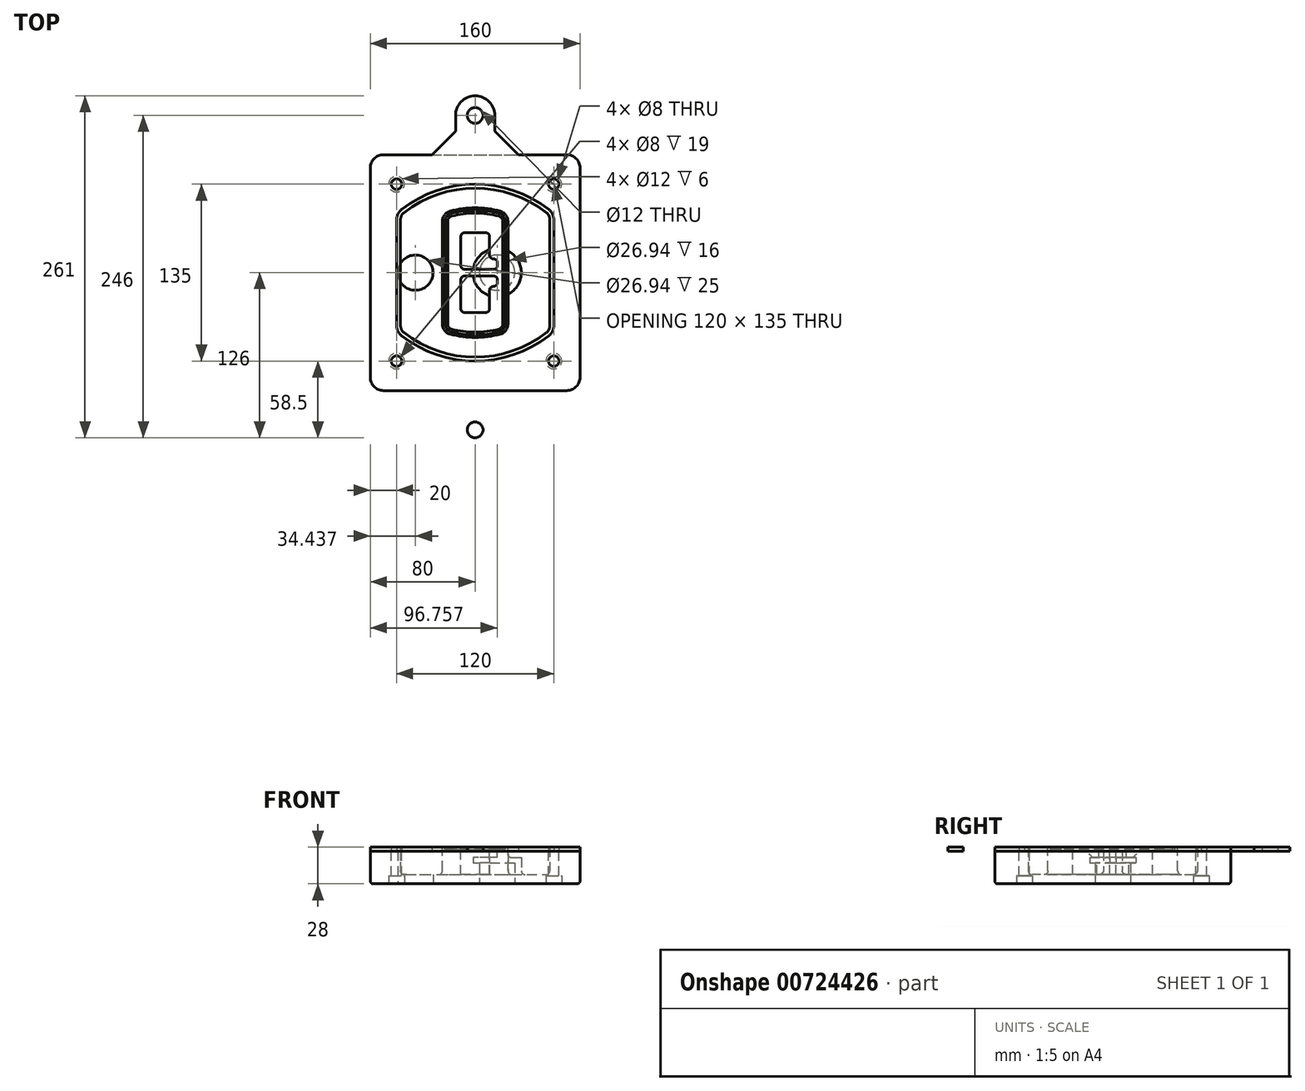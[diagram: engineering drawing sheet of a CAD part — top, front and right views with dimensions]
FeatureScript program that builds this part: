
annotation { "Feature Type Name" : "Feature", "Feature Type Description" : "" }
export const myFeature = defineFeature(function(context is Context, id is Id, definition is map)
    precondition{}
    {
        {
            var Q0;
            Q0=qCreatedBy(makeId("Top.planeOp"),FACE);
            var sketch = newSketch(context, id + "F0", { "sketchPlane" : qUnion([Q0])});
            skPoint(sketch, "E0.rect.middle", {"position": v(0, 0) * mm});
            skLineSegment(sketch, "E1.bottom", {"start": v(-70, -90) * mm, "end": v(70, -90) * mm});
            skLineSegment(sketch, "E1.top", {"start": v(-70, 90) * mm, "end": v(70, 90) * mm});
            skLineSegment(sketch, "E1.left", {"start": v(-80, -80) * mm, "end": v(-80, 80) * mm});
            skLineSegment(sketch, "E1.right", {"start": v(80, -80) * mm, "end": v(80, 80) * mm});
            skLineSegment(sketch, "E2", {"start": v(-80, 90) * mm, "end": v(80, -90) * mm, "construction": true});
            skLineSegment(sketch, "E3", {"start": v(80, 90) * mm, "end": v(-80, -90) * mm, "construction": true});
            skCircle(sketch, "E4", {"center": v(-60, 67.5) * mm, "radius": 4 * mm});
            skCircle(sketch, "E5", {"center": v(60, 67.5) * mm, "radius": 4 * mm});
            skCircle(sketch, "E6", {"center": v(60, -67.5) * mm, "radius": 4 * mm});
            skCircle(sketch, "E7", {"center": v(-60, -67.5) * mm, "radius": 4 * mm});
            skLineSegment(sketch, "E8", {"start": v(-60, 67.5) * mm, "end": v(60, 67.5) * mm, "construction": true});
            skLineSegment(sketch, "E9", {"start": v(60, 67.5) * mm, "end": v(60, -67.5) * mm, "construction": true});
            skLineSegment(sketch, "E10", {"start": v(60, -67.5) * mm, "end": v(-60, -67.5) * mm, "construction": true});
            skLineSegment(sketch, "E11", {"start": v(-60, -67.5) * mm, "end": v(-60, 67.5) * mm, "construction": true});
            skLineSegment(sketch, "E12", {"start": v(-60, 40.3) * mm, "end": v(-60, -40.3) * mm});
            skLineSegment(sketch, "E13", {"start": v(60, 40.3) * mm, "end": v(60, -40.3) * mm});
            skArc(sketch, "E14", {"start": v(56.15, 48.18) * mm, "mid": v(0, 67.5) * mm, "end": v(-56.15, 48.18) * mm});
            skArc(sketch, "E15", {"start": v(-56.15, -48.18) * mm, "mid": v(0, -67.5) * mm, "end": v(56.15, -48.18) * mm});
            skLineSegment(sketch, "E16", {"start": v(-60, 0) * mm, "end": v(60, 0) * mm, "construction": true});
            skPoint(sketch, "E17.visualSharp", {"position": v(-60, -45) * mm});
            skArc(sketch, "E17.filletArc", {"start": v(-60, -40.3) * mm, "mid": v(-58.99, -44.68) * mm, "end": v(-56.15, -48.18) * mm});
            skPoint(sketch, "E18.visualSharp", {"position": v(-60, 45) * mm});
            skArc(sketch, "E18.filletArc", {"start": v(-56.15, 48.18) * mm, "mid": v(-58.99, 44.68) * mm, "end": v(-60, 40.3) * mm});
            skPoint(sketch, "E19.visualSharp", {"position": v(60, 45) * mm});
            skArc(sketch, "E19.filletArc", {"start": v(60, 40.3) * mm, "mid": v(58.99, 44.68) * mm, "end": v(56.15, 48.18) * mm});
            skPoint(sketch, "E20.visualSharp", {"position": v(60, -45) * mm});
            skArc(sketch, "E20.filletArc", {"start": v(56.15, -48.18) * mm, "mid": v(58.99, -44.68) * mm, "end": v(60, -40.3) * mm});
            skPoint(sketch, "E21.visualSharp", {"position": v(-80, 90) * mm});
            skArc(sketch, "E21.filletArc", {"start": v(-70, 90) * mm, "mid": v(-77.07, 87.07) * mm, "end": v(-80, 80) * mm});
            skPoint(sketch, "E22.visualSharp", {"position": v(80, 90) * mm});
            skArc(sketch, "E22.filletArc", {"start": v(80, 80) * mm, "mid": v(77.07, 87.07) * mm, "end": v(70, 90) * mm});
            skPoint(sketch, "E23.visualSharp", {"position": v(80, -90) * mm});
            skArc(sketch, "E23.filletArc", {"start": v(70, -90) * mm, "mid": v(77.07, -87.07) * mm, "end": v(80, -80) * mm});
            skPoint(sketch, "E24.visualSharp", {"position": v(-80, -90) * mm});
            skArc(sketch, "E24.filletArc", {"start": v(-80, -80) * mm, "mid": v(-77.07, -87.07) * mm, "end": v(-70, -90) * mm});
            skArc(sketch, "E25.0", {"start": v(57, 40.3) * mm, "mid": v(56.3, 43.36) * mm, "end": v(54.3, 45.81) * mm});
            skLineSegment(sketch, "E25.1", {"start": v(57, 40.3) * mm, "end": v(57, -40.3) * mm});
            skArc(sketch, "E25.2", {"start": v(54.3, -45.81) * mm, "mid": v(56.3, -43.36) * mm, "end": v(57, -40.3) * mm});
            skArc(sketch, "E25.3", {"start": v(-54.3, -45.81) * mm, "mid": v(0, -64.5) * mm, "end": v(54.3, -45.81) * mm});
            skArc(sketch, "E25.4", {"start": v(-57, -40.3) * mm, "mid": v(-56.3, -43.36) * mm, "end": v(-54.3, -45.81) * mm});
            skArc(sketch, "E25.5", {"start": v(54.3, 45.81) * mm, "mid": v(0, 64.5) * mm, "end": v(-54.3, 45.81) * mm});
            skLineSegment(sketch, "E25.6", {"start": v(-57, 40.3) * mm, "end": v(-57, -40.3) * mm});
            skArc(sketch, "E25.7", {"start": v(-54.3, 45.81) * mm, "mid": v(-56.3, 43.36) * mm, "end": v(-57, 40.3) * mm});
            skArc(sketch, "E26.0", {"start": v(-58.62, 51.33) * mm, "mid": v(-62.58, 46.43) * mm, "end": v(-64, 40.3) * mm});
            skArc(sketch, "E26.1", {"start": v(58.62, 51.33) * mm, "mid": v(0, 71.5) * mm, "end": v(-58.62, 51.33) * mm});
            skArc(sketch, "E26.2", {"start": v(64, 40.3) * mm, "mid": v(62.58, 46.43) * mm, "end": v(58.62, 51.33) * mm});
            skLineSegment(sketch, "E26.3", {"start": v(64, 40.3) * mm, "end": v(64, -40.3) * mm});
            skArc(sketch, "E26.4", {"start": v(58.62, -51.33) * mm, "mid": v(62.58, -46.43) * mm, "end": v(64, -40.3) * mm});
            skLineSegment(sketch, "E26.5", {"start": v(-64, 40.3) * mm, "end": v(-64, -40.3) * mm});
            skArc(sketch, "E26.6", {"start": v(-58.62, -51.33) * mm, "mid": v(0, -71.5) * mm, "end": v(58.62, -51.33) * mm});
            skArc(sketch, "E26.7", {"start": v(-64, -40.3) * mm, "mid": v(-62.58, -46.43) * mm, "end": v(-58.62, -51.33) * mm});
            skSolve(sketch);
        }
        {
            var Q0;
            Q0=makeQuery(id+"F0.imprint","IMPRINT",FACE,{"disambiguationData":[TD([[makeQuery(id+"F0.imprint","IMPRINT",EDGE,{"derivedFrom":sQuery(id+"F0.wireOp",EDGE,"E1.bottom")}),1.0]])]});
            var Q1;
            Q1=makeQuery(id+"F0.imprint","IMPRINT",FACE,{"disambiguationData":[TD([[makeQuery(id+"F0.imprint","IMPRINT",EDGE,{"derivedFrom":sQuery(id+"F0.wireOp",EDGE,"E12")}),1.0]])]});
            var Q2;
            Q2=makeQuery(id+"F0.imprint","IMPRINT",FACE,{"disambiguationData":[TD([[makeQuery(id+"F0.imprint","IMPRINT",EDGE,{"derivedFrom":sQuery(id+"F0.wireOp",EDGE,"E25.0")}),1.0]])]});
            var Q3;
            Q3=makeQuery(id+"F0.imprint","IMPRINT",FACE,{"disambiguationData":[TD([[makeQuery(id+"F0.imprint","IMPRINT",EDGE,{"derivedFrom":sQuery(id+"F0.wireOp",EDGE,"E12")}),-1.0]])]});
            extrude(context, id + "F1", {"entities" : qUnion([Q0, Q1, Q2, Q3]), "oppositeDirection" : true, "depth" : 25 * mm});
        }
        {
            var Q0;
            Q0=makeQuery(id+"F0.imprint","IMPRINT",FACE,{"disambiguationData":[TD([[makeQuery(id+"F0.imprint","IMPRINT",EDGE,{"derivedFrom":sQuery(id+"F0.wireOp",EDGE,"E12")}),1.0]])]});
            extrude(context, id + "F2", {"entities" : qUnion([Q0]), "operationType" : NewBodyOperationType.ADD, "depth" : 3 * mm});
        }
        {
            var Q0;
            Q0=makeQuery(id+"F0.imprint","IMPRINT",FACE,{"disambiguationData":[TD([[makeQuery(id+"F0.imprint","IMPRINT",EDGE,{"derivedFrom":sQuery(id+"F0.wireOp",EDGE,"E25.0")}),1.0]])]});
            extrude(context, id + "F3", {"entities" : qUnion([Q0]), "operationType" : NewBodyOperationType.REMOVE, "oppositeDirection" : true, "depth" : 18 * mm});
        }
        {
            var Q0;
            Q0=makeQuery(id+"F2.opExtrude","CAP_FACE",FACE,{"disambiguationData":[OSD([sQuery(id+"F0.wireOp",EDGE,"E12"),sQuery(id+"F0.wireOp",EDGE,"E13"),sQuery(id+"F0.wireOp",EDGE,"E14"),sQuery(id+"F0.wireOp",EDGE,"E15"),sQuery(id+"F0.wireOp",EDGE,"E17.filletArc"),sQuery(id+"F0.wireOp",EDGE,"E18.filletArc"),sQuery(id+"F0.wireOp",EDGE,"E19.filletArc"),sQuery(id+"F0.wireOp",EDGE,"E20.filletArc"),sQuery(id+"F0.wireOp",EDGE,"E25.0"),sQuery(id+"F0.wireOp",EDGE,"E25.1"),sQuery(id+"F0.wireOp",EDGE,"E25.2"),sQuery(id+"F0.wireOp",EDGE,"E25.3"),sQuery(id+"F0.wireOp",EDGE,"E25.4"),sQuery(id+"F0.wireOp",EDGE,"E25.5"),sQuery(id+"F0.wireOp",EDGE,"E25.6"),sQuery(id+"F0.wireOp",EDGE,"E25.7")])],"isStart":false});
            var sketch = newSketch(context, id + "F4", { "sketchPlane" : qUnion([Q0])});
            skArc(sketch, "E27.0", {"start": v(-19.08, -46.97) * mm, "mid": v(0, -49.5) * mm, "end": v(19.08, -46.97) * mm});
            skArc(sketch, "E28.0", {"start": v(19.08, 46.97) * mm, "mid": v(0, 49.5) * mm, "end": v(-19.08, 46.97) * mm});
            skLineSegment(sketch, "E29", {"start": v(-25, 39.25) * mm, "end": v(-25, -39.25) * mm});
            skLineSegment(sketch, "E30", {"start": v(25, 39.25) * mm, "end": v(25, -39.25) * mm});
            skLineSegment(sketch, "E31", {"start": v(-25, 45.1) * mm, "end": v(25, 45.1) * mm, "construction": true});
            skLineSegment(sketch, "E32", {"start": v(-25, -45.1) * mm, "end": v(25, -45.1) * mm, "construction": true});
            skPoint(sketch, "E33.visualSharp", {"position": v(-25, 45.1) * mm});
            skArc(sketch, "E33.filletArc", {"start": v(-19.08, 46.97) * mm, "mid": v(-23.35, 44.11) * mm, "end": v(-25, 39.25) * mm});
            skPoint(sketch, "E34.visualSharp", {"position": v(25, 45.1) * mm});
            skArc(sketch, "E34.filletArc", {"start": v(25, 39.25) * mm, "mid": v(23.35, 44.11) * mm, "end": v(19.08, 46.97) * mm});
            skPoint(sketch, "E35.visualSharp", {"position": v(25, -45.1) * mm});
            skArc(sketch, "E35.filletArc", {"start": v(19.08, -46.97) * mm, "mid": v(23.35, -44.11) * mm, "end": v(25, -39.25) * mm});
            skPoint(sketch, "E36.visualSharp", {"position": v(-25, -45.1) * mm});
            skArc(sketch, "E36.filletArc", {"start": v(-25, -39.25) * mm, "mid": v(-23.35, -44.11) * mm, "end": v(-19.08, -46.97) * mm});
            skArc(sketch, "E37.0", {"start": v(54.3, 45.81) * mm, "mid": v(0, 64.5) * mm, "end": v(-54.3, 45.81) * mm});
            skArc(sketch, "E37.1", {"start": v(-54.3, 45.81) * mm, "mid": v(-56.3, 43.36) * mm, "end": v(-57, 40.3) * mm});
            skLineSegment(sketch, "E37.2", {"start": v(-57, 40.3) * mm, "end": v(-57, -40.3) * mm});
            skArc(sketch, "E37.3", {"start": v(-57, -40.3) * mm, "mid": v(-56.3, -43.36) * mm, "end": v(-54.3, -45.81) * mm});
            skArc(sketch, "E37.4", {"start": v(-54.3, -45.81) * mm, "mid": v(0, -64.5) * mm, "end": v(54.3, -45.81) * mm});
            skArc(sketch, "E37.5", {"start": v(54.3, -45.81) * mm, "mid": v(56.3, -43.36) * mm, "end": v(57, -40.3) * mm});
            skLineSegment(sketch, "E37.6", {"start": v(57, 40.3) * mm, "end": v(57, -40.3) * mm});
            skArc(sketch, "E37.7", {"start": v(57, 40.3) * mm, "mid": v(56.3, 43.36) * mm, "end": v(54.3, 45.81) * mm});
            skLineSegment(sketch, "E38.0", {"start": v(23, 39.25) * mm, "end": v(23, -39.25) * mm});
            skArc(sketch, "E38.1", {"start": v(18.56, -45.04) * mm, "mid": v(21.76, -42.9) * mm, "end": v(23, -39.25) * mm});
            skArc(sketch, "E38.2", {"start": v(-18.56, -45.04) * mm, "mid": v(0, -47.5) * mm, "end": v(18.56, -45.04) * mm});
            skArc(sketch, "E38.3", {"start": v(-23, -39.25) * mm, "mid": v(-21.76, -42.9) * mm, "end": v(-18.56, -45.04) * mm});
            skLineSegment(sketch, "E38.4", {"start": v(-23, 39.25) * mm, "end": v(-23, -39.25) * mm});
            skArc(sketch, "E38.5", {"start": v(23, 39.25) * mm, "mid": v(21.76, 42.9) * mm, "end": v(18.56, 45.04) * mm});
            skArc(sketch, "E38.6", {"start": v(-18.56, 45.04) * mm, "mid": v(-21.76, 42.9) * mm, "end": v(-23, 39.25) * mm});
            skArc(sketch, "E38.7", {"start": v(18.56, 45.04) * mm, "mid": v(0, 47.5) * mm, "end": v(-18.56, 45.04) * mm});
            skArc(sketch, "E39.0", {"start": v(21, 39.25) * mm, "mid": v(20.18, 41.68) * mm, "end": v(18.04, 43.1) * mm});
            skLineSegment(sketch, "E39.1", {"start": v(21, 39.25) * mm, "end": v(21, -39.25) * mm});
            skArc(sketch, "E39.2", {"start": v(18.04, -43.1) * mm, "mid": v(20.18, -41.68) * mm, "end": v(21, -39.25) * mm});
            skArc(sketch, "E39.3", {"start": v(-18.04, -43.1) * mm, "mid": v(0, -45.5) * mm, "end": v(18.04, -43.1) * mm});
            skArc(sketch, "E39.4", {"start": v(-21, -39.25) * mm, "mid": v(-20.18, -41.68) * mm, "end": v(-18.04, -43.1) * mm});
            skArc(sketch, "E39.5", {"start": v(18.04, 43.1) * mm, "mid": v(0, 45.5) * mm, "end": v(-18.04, 43.1) * mm});
            skLineSegment(sketch, "E39.6", {"start": v(-21, 39.25) * mm, "end": v(-21, -39.25) * mm});
            skArc(sketch, "E39.7", {"start": v(-18.04, 43.1) * mm, "mid": v(-20.18, 41.68) * mm, "end": v(-21, 39.25) * mm});
            skLineSegment(sketch, "E40", {"start": v(-25, 0) * mm, "end": v(25, 0) * mm, "construction": true});
            skLineSegment(sketch, "E41", {"start": v(-11, 5.5) * mm, "end": v(-11, 27.5) * mm});
            skLineSegment(sketch, "E42", {"start": v(-8, 30.5) * mm, "end": v(8, 30.5) * mm});
            skLineSegment(sketch, "E43", {"start": v(11, 27.5) * mm, "end": v(11, 13.5) * mm});
            skLineSegment(sketch, "E44", {"start": v(14, 10.5) * mm, "end": v(14, 10.5) * mm});
            skLineSegment(sketch, "E45", {"start": v(17, 7.5) * mm, "end": v(17, 5.5) * mm});
            skLineSegment(sketch, "E46", {"start": v(14, 2.5) * mm, "end": v(-8, 2.5) * mm});
            skPoint(sketch, "E47.visualSharp", {"position": v(-11, 30.5) * mm});
            skArc(sketch, "E47.filletArc", {"start": v(-8, 30.5) * mm, "mid": v(-10.12, 29.62) * mm, "end": v(-11, 27.5) * mm});
            skPoint(sketch, "E48.visualSharp", {"position": v(11, 30.5) * mm});
            skArc(sketch, "E48.filletArc", {"start": v(11, 27.5) * mm, "mid": v(10.12, 29.62) * mm, "end": v(8, 30.5) * mm});
            skPoint(sketch, "E49.visualSharp", {"position": v(11, 10.5) * mm});
            skArc(sketch, "E49.filletArc", {"start": v(11, 13.5) * mm, "mid": v(11.88, 11.38) * mm, "end": v(14, 10.5) * mm});
            skPoint(sketch, "E50.visualSharp", {"position": v(17, 10.5) * mm});
            skArc(sketch, "E50.filletArc", {"start": v(17, 7.5) * mm, "mid": v(16.12, 9.62) * mm, "end": v(14, 10.5) * mm});
            skPoint(sketch, "E51.visualSharp", {"position": v(17, 2.5) * mm});
            skArc(sketch, "E51.filletArc", {"start": v(14, 2.5) * mm, "mid": v(16.12, 3.38) * mm, "end": v(17, 5.5) * mm});
            skPoint(sketch, "E52.visualSharp", {"position": v(-11, 2.5) * mm});
            skArc(sketch, "E52.filletArc", {"start": v(-11, 5.5) * mm, "mid": v(-10.12, 3.38) * mm, "end": v(-8, 2.5) * mm});
            skLineSegment(sketch, "E53.0.MirrorCS", {"start": v(14, -2.5) * mm, "end": v(-8, -2.5) * mm});
            skArc(sketch, "E54.0.MirrorCS", {"start": v(-11, -5.5) * mm, "mid": v(-10.12, -3.38) * mm, "end": v(-8, -2.5) * mm});
            skLineSegment(sketch, "E55.0.MirrorCS", {"start": v(-11, -5.5) * mm, "end": v(-11, -27.5) * mm});
            skArc(sketch, "E56.0.MirrorCS", {"start": v(-8, -30.5) * mm, "mid": v(-10.12, -29.62) * mm, "end": v(-11, -27.5) * mm});
            skLineSegment(sketch, "E57.0.MirrorCS", {"start": v(-8, -30.5) * mm, "end": v(8, -30.5) * mm});
            skArc(sketch, "E58.0.MirrorCS", {"start": v(11, -27.5) * mm, "mid": v(10.12, -29.62) * mm, "end": v(8, -30.5) * mm});
            skLineSegment(sketch, "E59.0.MirrorCS", {"start": v(11, -27.5) * mm, "end": v(11, -13.5) * mm});
            skArc(sketch, "E60.0.MirrorCS", {"start": v(11, -13.5) * mm, "mid": v(11.88, -11.38) * mm, "end": v(14, -10.5) * mm});
            skArc(sketch, "E61.0.MirrorCS", {"start": v(17, -7.5) * mm, "mid": v(16.12, -9.62) * mm, "end": v(14, -10.5) * mm});
            skLineSegment(sketch, "E62.0.MirrorCS", {"start": v(17, -7.5) * mm, "end": v(17, -5.5) * mm});
            skArc(sketch, "E63.0.MirrorCS", {"start": v(14, -2.5) * mm, "mid": v(16.12, -3.38) * mm, "end": v(17, -5.5) * mm});
            skSolve(sketch);
        }
        {
            var Q0;
            Q0=makeQuery(id+"F4.imprint","IMPRINT",FACE,{"disambiguationData":[TD([[makeQuery(id+"F4.imprint","IMPRINT",EDGE,{"derivedFrom":sQuery(id+"F4.wireOp",EDGE,"E27.0")}),1.0]])]});
            var Q1;
            Q1=makeQuery(id+"F4.imprint","IMPRINT",FACE,{"disambiguationData":[TD([[makeQuery(id+"F4.imprint","IMPRINT",EDGE,{"derivedFrom":sQuery(id+"F4.wireOp",EDGE,"E38.0")}),-1.0]])]});
            var Q2;
            Q2=makeQuery(id+"F4.imprint","IMPRINT",FACE,{"disambiguationData":[TD([[makeQuery(id+"F4.imprint","IMPRINT",EDGE,{"derivedFrom":sQuery(id+"F4.wireOp",EDGE,"E39.0")}),1.0]])]});
            extrude(context, id + "F5", {"entities" : qUnion([Q0, Q1, Q2]), "operationType" : NewBodyOperationType.ADD, "endBound" : BoundingType.UP_TO_NEXT, "oppositeDirection" : true, "depth" : 25 * mm});
        }
        {
            var Q0;
            Q0=makeQuery(id+"F4.imprint","IMPRINT",FACE,{"disambiguationData":[TD([[makeQuery(id+"F4.imprint","IMPRINT",EDGE,{"derivedFrom":sQuery(id+"F4.wireOp",EDGE,"E38.0")}),-1.0]])]});
            extrude(context, id + "F6", {"entities" : qUnion([Q0]), "operationType" : NewBodyOperationType.REMOVE, "oppositeDirection" : true, "depth" : 2 * mm});
        }
        {
            var Q0;
            Q0=makeQuery(id+"F1.opExtrude","CAP_FACE",FACE,{"disambiguationData":[OSD([sQuery(id+"F0.wireOp",EDGE,"E1.bottom"),sQuery(id+"F0.wireOp",EDGE,"E1.top"),sQuery(id+"F0.wireOp",EDGE,"E1.left"),sQuery(id+"F0.wireOp",EDGE,"E1.right"),sQuery(id+"F0.wireOp",EDGE,"E4"),sQuery(id+"F0.wireOp",EDGE,"E5"),sQuery(id+"F0.wireOp",EDGE,"E6"),sQuery(id+"F0.wireOp",EDGE,"E7"),sQuery(id+"F0.wireOp",EDGE,"E21.filletArc"),sQuery(id+"F0.wireOp",EDGE,"E22.filletArc"),sQuery(id+"F0.wireOp",EDGE,"E23.filletArc"),sQuery(id+"F0.wireOp",EDGE,"E24.filletArc")])],"isStart":false});
            var sketch = newSketch(context, id + "F7", { "sketchPlane" : qUnion([Q0])});
            skCircle(sketch, "E64", {"center": v(16.76, 0) * mm, "radius": 13.47 * mm});
            skCircle(sketch, "E65", {"center": v(-45.56, 0) * mm, "radius": 13.47 * mm});
            skLineSegment(sketch, "E66", {"start": v(80, 0) * mm, "end": v(-80, 0) * mm});
            skCircle(sketch, "E67", {"center": v(16.76, 0) * mm, "radius": 18.47 * mm});
            skCircle(sketch, "E68", {"center": v(60, -67.5) * mm, "radius": 6 * mm});
            skCircle(sketch, "E69", {"center": v(-60, -67.5) * mm, "radius": 6 * mm});
            skCircle(sketch, "E70", {"center": v(-60, 67.5) * mm, "radius": 6 * mm});
            skCircle(sketch, "E71", {"center": v(60, 67.5) * mm, "radius": 6 * mm});
            skSolve(sketch);
        }
        {
            var Q0;
            {var subQ1=sQuery(id+"F7.wireOp",EDGE,"E66");var subQ4=sQuery(id+"F7.wireOp",EDGE,"E64");var subQ6=makeQuery(id+"F7.imprint","INTERSECT",VERTEX,{"disambiguationData":[OD(0.0)],"derivedFrom":[subQ4,subQ1]});Q0=makeQuery(id+"F7.imprint","IMPRINT",FACE,{"disambiguationData":[TD([[makeQuery(id+"F7.imprint","IMPRINT",EDGE,{"disambiguationData":[TD([[subQ6,-1.0]])],"derivedFrom":subQ4}),-1.0]])]});}
            var Q1;
            {var subQ0=sQuery(id+"F7.wireOp",EDGE,"E66");var subQ1=sQuery(id+"F7.wireOp",EDGE,"E64");var subQ3=makeQuery(id+"F7.imprint","INTERSECT",VERTEX,{"disambiguationData":[OD(0.0)],"derivedFrom":[subQ1,subQ0]});Q1=makeQuery(id+"F7.imprint","IMPRINT",FACE,{"disambiguationData":[TD([[makeQuery(id+"F7.imprint","IMPRINT",EDGE,{"disambiguationData":[TD([[subQ3,-1.0]])],"derivedFrom":subQ1}),1.0]])]});}
            var Q2;
            {var subQ0=sQuery(id+"F7.wireOp",EDGE,"E66");var subQ1=sQuery(id+"F7.wireOp",EDGE,"E64");var subQ3=makeQuery(id+"F7.imprint","INTERSECT",VERTEX,{"disambiguationData":[OD(0.0)],"derivedFrom":[subQ1,subQ0]});Q2=makeQuery(id+"F7.imprint","IMPRINT",FACE,{"disambiguationData":[TD([[makeQuery(id+"F7.imprint","IMPRINT",EDGE,{"disambiguationData":[TD([[subQ3,1.0]])],"derivedFrom":subQ1}),1.0]])]});}
            var Q3;
            {var subQ1=sQuery(id+"F7.wireOp",EDGE,"E66");var subQ4=sQuery(id+"F7.wireOp",EDGE,"E64");var subQ6=makeQuery(id+"F7.imprint","INTERSECT",VERTEX,{"disambiguationData":[OD(0.0)],"derivedFrom":[subQ4,subQ1]});Q3=makeQuery(id+"F7.imprint","IMPRINT",FACE,{"disambiguationData":[TD([[makeQuery(id+"F7.imprint","IMPRINT",EDGE,{"disambiguationData":[TD([[subQ6,1.0]])],"derivedFrom":subQ4}),-1.0]])]});}
            extrude(context, id + "F8", {"entities" : qUnion([Q0, Q1, Q2, Q3]), "operationType" : NewBodyOperationType.ADD, "oppositeDirection" : true, "depth" : 20 * mm});
        }
        {
            var Q0;
            {var subQ0=sQuery(id+"F7.wireOp",EDGE,"E66");var subQ1=sQuery(id+"F7.wireOp",EDGE,"E64");var subQ3=makeQuery(id+"F7.imprint","INTERSECT",VERTEX,{"disambiguationData":[OD(0.0)],"derivedFrom":[subQ1,subQ0]});Q0=makeQuery(id+"F7.imprint","IMPRINT",FACE,{"disambiguationData":[TD([[makeQuery(id+"F7.imprint","IMPRINT",EDGE,{"disambiguationData":[TD([[subQ3,-1.0]])],"derivedFrom":subQ1}),1.0]])]});}
            var Q1;
            {var subQ0=sQuery(id+"F7.wireOp",EDGE,"E66");var subQ1=sQuery(id+"F7.wireOp",EDGE,"E64");var subQ3=makeQuery(id+"F7.imprint","INTERSECT",VERTEX,{"disambiguationData":[OD(0.0)],"derivedFrom":[subQ1,subQ0]});Q1=makeQuery(id+"F7.imprint","IMPRINT",FACE,{"disambiguationData":[TD([[makeQuery(id+"F7.imprint","IMPRINT",EDGE,{"disambiguationData":[TD([[subQ3,1.0]])],"derivedFrom":subQ1}),1.0]])]});}
            extrude(context, id + "F9", {"entities" : qUnion([Q0, Q1]), "operationType" : NewBodyOperationType.REMOVE, "oppositeDirection" : true, "depth" : 16 * mm});
        }
        {
            var Q0;
            {var subQ0=sQuery(id+"F7.wireOp",EDGE,"E66");var subQ1=sQuery(id+"F7.wireOp",EDGE,"E65");var subQ3=makeQuery(id+"F7.imprint","INTERSECT",VERTEX,{"disambiguationData":[OD(0.0)],"derivedFrom":[subQ1,subQ0]});Q0=makeQuery(id+"F7.imprint","IMPRINT",FACE,{"disambiguationData":[TD([[makeQuery(id+"F7.imprint","IMPRINT",EDGE,{"disambiguationData":[TD([[subQ3,-1.0]])],"derivedFrom":subQ1}),1.0]])]});}
            var Q1;
            {var subQ0=sQuery(id+"F7.wireOp",EDGE,"E66");var subQ1=sQuery(id+"F7.wireOp",EDGE,"E65");var subQ3=makeQuery(id+"F7.imprint","INTERSECT",VERTEX,{"disambiguationData":[OD(0.0)],"derivedFrom":[subQ1,subQ0]});Q1=makeQuery(id+"F7.imprint","IMPRINT",FACE,{"disambiguationData":[TD([[makeQuery(id+"F7.imprint","IMPRINT",EDGE,{"disambiguationData":[TD([[subQ3,1.0]])],"derivedFrom":subQ1}),1.0]])]});}
            extrude(context, id + "F10", {"entities" : qUnion([Q0, Q1]), "operationType" : NewBodyOperationType.REMOVE, "oppositeDirection" : true, "depth" : 25 * mm});
        }
        {
            var Q0;
            Q0=makeQuery(id+"F7.imprint","IMPRINT",FACE,{"disambiguationData":[TD([[makeQuery(id+"F7.imprint","IMPRINT",EDGE,{"derivedFrom":sQuery(id+"F7.wireOp",EDGE,"E68")}),1.0]])]});
            var Q1;
            Q1=makeQuery(id+"F7.imprint","IMPRINT",FACE,{"disambiguationData":[TD([[makeQuery(id+"F7.imprint","IMPRINT",EDGE,{"derivedFrom":makeQuery(id+"F1.opExtrude","CAP_EDGE",EDGE,{"disambiguationData":[OSD([sQuery(id+"F0.wireOp",EDGE,"E5")])],"isStart":false})}),-1.0]])]});
            var Q2;
            Q2=makeQuery(id+"F7.imprint","IMPRINT",FACE,{"disambiguationData":[TD([[makeQuery(id+"F7.imprint","IMPRINT",EDGE,{"derivedFrom":sQuery(id+"F7.wireOp",EDGE,"E69")}),1.0]])]});
            var Q3;
            Q3=makeQuery(id+"F7.imprint","IMPRINT",FACE,{"disambiguationData":[TD([[makeQuery(id+"F7.imprint","IMPRINT",EDGE,{"derivedFrom":makeQuery(id+"F1.opExtrude","CAP_EDGE",EDGE,{"disambiguationData":[OSD([sQuery(id+"F0.wireOp",EDGE,"E4")])],"isStart":false})}),-1.0]])]});
            var Q4;
            Q4=makeQuery(id+"F7.imprint","IMPRINT",FACE,{"disambiguationData":[TD([[makeQuery(id+"F7.imprint","IMPRINT",EDGE,{"derivedFrom":sQuery(id+"F7.wireOp",EDGE,"E70")}),1.0]])]});
            var Q5;
            Q5=makeQuery(id+"F7.imprint","IMPRINT",FACE,{"disambiguationData":[TD([[makeQuery(id+"F7.imprint","IMPRINT",EDGE,{"derivedFrom":makeQuery(id+"F1.opExtrude","CAP_EDGE",EDGE,{"disambiguationData":[OSD([sQuery(id+"F0.wireOp",EDGE,"E7")])],"isStart":false})}),-1.0]])]});
            var Q6;
            Q6=makeQuery(id+"F7.imprint","IMPRINT",FACE,{"disambiguationData":[TD([[makeQuery(id+"F7.imprint","IMPRINT",EDGE,{"derivedFrom":sQuery(id+"F7.wireOp",EDGE,"E71")}),1.0]])]});
            var Q7;
            Q7=makeQuery(id+"F7.imprint","IMPRINT",FACE,{"disambiguationData":[TD([[makeQuery(id+"F7.imprint","IMPRINT",EDGE,{"derivedFrom":makeQuery(id+"F1.opExtrude","CAP_EDGE",EDGE,{"disambiguationData":[OSD([sQuery(id+"F0.wireOp",EDGE,"E6")])],"isStart":false})}),-1.0]])]});
            extrude(context, id + "F11", {"entities" : qUnion([Q0, Q1, Q2, Q3, Q4, Q5, Q6, Q7]), "operationType" : NewBodyOperationType.REMOVE, "oppositeDirection" : true, "depth" : 6 * mm});
        }
        {
            var Q0;
            Q0=makeQuery(id+"F9.boolean.opBoolean","COPY",FACE,{"derivedFrom":makeQuery(id+"F9.opExtrude","CAP_FACE",FACE,{"disambiguationData":[OSD([sQuery(id+"F7.wireOp",EDGE,"E64")])],"isStart":false})});
            var sketch = newSketch(context, id + "F12", { "sketchPlane" : qUnion([Q0])});
            skArc(sketch, "E72.0", {"start": v(11, 17.55) * mm, "mid": v(2.57, 11.82) * mm, "end": v(-1.54, 2.5) * mm});
            skArc(sketch, "E72.1", {"start": v(-1.54, -2.5) * mm, "mid": v(2.57, -11.82) * mm, "end": v(11, -17.55) * mm});
            skLineSegment(sketch, "E73", {"start": v(-1.54, -2.5) * mm, "end": v(14, -2.5) * mm});
            skLineSegment(sketch, "E74.0", {"start": v(14, 2.5) * mm, "end": v(-1.54, 2.5) * mm});
            skArc(sketch, "E74.1", {"start": v(14, 2.5) * mm, "mid": v(16.12, 3.38) * mm, "end": v(17, 5.5) * mm});
            skLineSegment(sketch, "E74.2", {"start": v(17, 7.5) * mm, "end": v(17, 5.5) * mm});
            skArc(sketch, "E74.3", {"start": v(17, 7.5) * mm, "mid": v(16.12, 9.62) * mm, "end": v(14, 10.5) * mm});
            skArc(sketch, "E74.4", {"start": v(11, 13.5) * mm, "mid": v(11.88, 11.38) * mm, "end": v(14, 10.5) * mm});
            skLineSegment(sketch, "E74.5", {"start": v(11, 17.55) * mm, "end": v(11, 13.5) * mm});
            skLineSegment(sketch, "E74.7", {"start": v(14, -2.5) * mm, "end": v(-1.54, -2.5) * mm});
            skArc(sketch, "E74.8", {"start": v(14, -2.5) * mm, "mid": v(16.12, -3.38) * mm, "end": v(17, -5.5) * mm});
            skLineSegment(sketch, "E74.9", {"start": v(17, -7.5) * mm, "end": v(17, -5.5) * mm});
            skArc(sketch, "E74.10", {"start": v(17, -7.5) * mm, "mid": v(16.12, -9.62) * mm, "end": v(14, -10.5) * mm});
            skArc(sketch, "E74.11", {"start": v(11, -13.5) * mm, "mid": v(11.88, -11.38) * mm, "end": v(14, -10.5) * mm});
            skLineSegment(sketch, "E74.12", {"start": v(11, -17.55) * mm, "end": v(11, -13.5) * mm});
            skPoint(sketch, "E75.orphan", {"position": v(11, -27.5) * mm});
            skPoint(sketch, "E76.orphan", {"position": v(-8, -2.5) * mm});
            skPoint(sketch, "E77.orphan", {"position": v(-8, 2.5) * mm});
            skPoint(sketch, "E78.orphan", {"position": v(11, 27.5) * mm});
            skSolve(sketch);
        }
        {
            var Q0;
            {var subQ7=sQuery(id+"F12.wireOp",EDGE,"E72.0");var subQ14=sQuery(id+"F12.wireOp",EDGE,"E72.1");var subQ16=sQuery(id+"F12.wireOp",EDGE,"E74.1");var subQ18=sQuery(id+"F12.wireOp",EDGE,"E74.8");Q0=qUnion([makeQuery(id+"F12.imprint","IMPRINT",FACE,{"disambiguationData":[TD([[makeQuery(id+"F12.imprint","IMPRINT",EDGE,{"derivedFrom":subQ7}),1.0]])]}),makeQuery(id+"F12.imprint","IMPRINT",FACE,{"disambiguationData":[TD([[makeQuery(id+"F12.imprint","IMPRINT",EDGE,{"derivedFrom":subQ14}),1.0]])]}),makeQuery(id+"F12.imprint","IMPRINT",FACE,{"disambiguationData":[TD([[makeQuery(id+"F12.imprint","IMPRINT",EDGE,{"derivedFrom":subQ16}),1.0]])]}),makeQuery(id+"F12.imprint","IMPRINT",FACE,{"disambiguationData":[TD([[makeQuery(id+"F12.imprint","IMPRINT",EDGE,{"derivedFrom":subQ18}),-1.0]])]})]);}
            var Q1;
            Q1=makeQuery(id+"F5.boolean.opBoolean","SPLIT",FACE,{"disambiguationData":[TD([makeQuery(id+"F5.opExtrude","SWEPT_FACE",FACE,{"disambiguationData":[OSD([sQuery(id+"F4.wireOp",EDGE,"E41")])]})])],"derivedFrom":makeQuery(id+"F3.boolean.opBoolean","COPY",FACE,{"derivedFrom":makeQuery(id+"F3.opExtrude","CAP_FACE",FACE,{"disambiguationData":[OSD([sQuery(id+"F0.wireOp",EDGE,"E25.0"),sQuery(id+"F0.wireOp",EDGE,"E25.1"),sQuery(id+"F0.wireOp",EDGE,"E25.2"),sQuery(id+"F0.wireOp",EDGE,"E25.3"),sQuery(id+"F0.wireOp",EDGE,"E25.4"),sQuery(id+"F0.wireOp",EDGE,"E25.5"),sQuery(id+"F0.wireOp",EDGE,"E25.6"),sQuery(id+"F0.wireOp",EDGE,"E25.7")])],"isStart":false})})});
            extrude(context, id + "F13", {"entities" : qUnion([Q0]), "operationType" : NewBodyOperationType.REMOVE, "endBound" : BoundingType.UP_TO_SURFACE, "endBoundEntityFace" : qUnion([Q1]), "depth" : 25 * mm});
        }
        {
            var Q0;
            Q0=makeQuery(id+"F3.boolean.opBoolean","COPY",EDGE,{"derivedFrom":makeQuery(id+"F3.opExtrude","CAP_EDGE",EDGE,{"disambiguationData":[OSD([sQuery(id+"F0.wireOp",EDGE,"E25.6")])],"isStart":false})});
            var Q1;
            Q1=makeQuery(id+"F8.boolean.opBoolean","INTERSECT",EDGE,{"derivedFrom":[makeQuery(id+"F5.opExtrude","SWEPT_FACE",FACE,{"disambiguationData":[OSD([sQuery(id+"F4.wireOp",EDGE,"E30")])]}),makeQuery(id+"F8.opExtrude","CAP_FACE",FACE,{"disambiguationData":[OSD([sQuery(id+"F7.wireOp",EDGE,"E67")])],"isStart":false})]});
            var Q2;
            Q2=makeQuery(id+"F8.boolean.opBoolean","INTERSECT",EDGE,{"disambiguationData":[OD(1.0)],"derivedFrom":[makeQuery(id+"F5.opExtrude","SWEPT_FACE",FACE,{"disambiguationData":[OSD([sQuery(id+"F4.wireOp",EDGE,"E30")])]}),makeQuery(id+"F8.opExtrude","SWEPT_FACE",FACE,{"disambiguationData":[OSD([sQuery(id+"F7.wireOp",EDGE,"E67")])]})]});
            var Q3;
            {var subQ0=sQuery(id+"F4.wireOp",EDGE,"E30");Q3=makeQuery(id+"F8.boolean.opBoolean","SPLIT",EDGE,{"disambiguationData":[TD([makeQuery(id+"F5.opExtrude","SWEPT_FACE",FACE,{"disambiguationData":[OSD([sQuery(id+"F4.wireOp",EDGE,"E35.filletArc")])]})])],"derivedFrom":makeQuery(id+"F5.opExtrude","CAP_EDGE",EDGE,{"disambiguationData":[OSD([subQ0])],"isStart":false})});}
            var Q4;
            {var subQ0=sQuery(id+"F0.wireOp",EDGE,"E25.7");var subQ1=sQuery(id+"F0.wireOp",EDGE,"E25.1");var subQ2=sQuery(id+"F0.wireOp",EDGE,"E25.6");var subQ3=sQuery(id+"F0.wireOp",EDGE,"E25.5");var subQ4=sQuery(id+"F0.wireOp",EDGE,"E25.4");var subQ5=sQuery(id+"F0.wireOp",EDGE,"E25.0");var subQ6=sQuery(id+"F0.wireOp",EDGE,"E25.2");var subQ7=sQuery(id+"F0.wireOp",EDGE,"E25.3");Q4=makeQuery(id+"F8.boolean.opBoolean","INTERSECT",EDGE,{"derivedFrom":[makeQuery(id+"F5.boolean.opBoolean","SPLIT",FACE,{"disambiguationData":[TD([makeQuery(id+"F2.opExtrude","SWEPT_FACE",FACE,{"disambiguationData":[OSD([subQ5])]})])],"derivedFrom":makeQuery(id+"F3.boolean.opBoolean","COPY",FACE,{"derivedFrom":makeQuery(id+"F3.opExtrude","CAP_FACE",FACE,{"disambiguationData":[OSD([subQ5,subQ1,subQ6,subQ7,subQ4,subQ3,subQ2,subQ0])],"isStart":false})})}),makeQuery(id+"F8.opExtrude","SWEPT_FACE",FACE,{"disambiguationData":[OSD([sQuery(id+"F7.wireOp",EDGE,"E67")])]})]});}
            var Q5;
            Q5=makeQuery(id+"F8.boolean.opBoolean","INTERSECT",EDGE,{"disambiguationData":[OD(0.0)],"derivedFrom":[makeQuery(id+"F5.opExtrude","SWEPT_FACE",FACE,{"disambiguationData":[OSD([sQuery(id+"F4.wireOp",EDGE,"E30")])]}),makeQuery(id+"F8.opExtrude","SWEPT_FACE",FACE,{"disambiguationData":[OSD([sQuery(id+"F7.wireOp",EDGE,"E67")])]})]});
            fillet(context, id + "F14", {"entities" : qUnion([Q0, Q1, Q2, Q3, Q4, Q5]), "radius" : 3 * mm, "tangentPropagation" : true, "allowEdgeOverflow" : false});
        }
        {
            var Q0;
            Q0=makeQuery(id+"F1.opExtrude","CAP_EDGE",EDGE,{"disambiguationData":[OSD([sQuery(id+"F0.wireOp",EDGE,"E1.bottom")])],"isStart":false});
            fillet(context, id + "F15", {"entities" : qUnion([Q0]), "radius" : 2 * mm, "tangentPropagation" : true, "allowEdgeOverflow" : false});
        }
        {
            var Q0;
            {var subQ0=sQuery(id+"F0.wireOp",EDGE,"E21.filletArc");var subQ1=sQuery(id+"F0.wireOp",EDGE,"E7");var subQ2=sQuery(id+"F0.wireOp",EDGE,"E6");var subQ3=sQuery(id+"F0.wireOp",EDGE,"E5");var subQ4=sQuery(id+"F0.wireOp",EDGE,"E4");var subQ5=sQuery(id+"F0.wireOp",EDGE,"E22.filletArc");var subQ6=sQuery(id+"F0.wireOp",EDGE,"E1.bottom");var subQ7=sQuery(id+"F0.wireOp",EDGE,"E1.right");var subQ8=sQuery(id+"F0.wireOp",EDGE,"E1.top");var subQ9=sQuery(id+"F0.wireOp",EDGE,"E1.left");var subQ10=sQuery(id+"F0.wireOp",EDGE,"E23.filletArc");var subQ11=sQuery(id+"F0.wireOp",EDGE,"E24.filletArc");Q0=makeQuery(id+"F2.boolean.opBoolean","SPLIT",FACE,{"disambiguationData":[TD([makeQuery(id+"F1.opExtrude","SWEPT_FACE",FACE,{"disambiguationData":[OSD([subQ6])]})])],"derivedFrom":makeQuery(id+"F1.opExtrude","CAP_FACE",FACE,{"disambiguationData":[OSD([subQ6,subQ8,subQ9,subQ7,subQ4,subQ3,subQ2,subQ1,subQ0,subQ5,subQ10,subQ11])],"isStart":true})});}
            var sketch = newSketch(context, id + "F16", { "sketchPlane" : qUnion([Q0])});
            skLineSegment(sketch, "E79.0", {"start": v(-70, 90) * mm, "end": v(70, 90) * mm});
            skArc(sketch, "E79.1", {"start": v(-70, 90) * mm, "mid": v(-77.07, 87.07) * mm, "end": v(-80, 80) * mm});
            skLineSegment(sketch, "E79.2", {"start": v(-80, -80) * mm, "end": v(-80, 80) * mm});
            skArc(sketch, "E79.3", {"start": v(-80, -80) * mm, "mid": v(-77.07, -87.07) * mm, "end": v(-70, -90) * mm});
            skLineSegment(sketch, "E79.4", {"start": v(-70, -90) * mm, "end": v(70, -90) * mm});
            skArc(sketch, "E79.5", {"start": v(70, -90) * mm, "mid": v(77.07, -87.07) * mm, "end": v(80, -80) * mm});
            skLineSegment(sketch, "E79.6", {"start": v(80, -80) * mm, "end": v(80, 80) * mm});
            skArc(sketch, "E79.7", {"start": v(80, 80) * mm, "mid": v(77.07, 87.07) * mm, "end": v(70, 90) * mm});
            skCircle(sketch, "E79.8", {"center": v(60, 67.5) * mm, "radius": 4 * mm});
            skCircle(sketch, "E79.9", {"center": v(-60, 67.5) * mm, "radius": 4 * mm});
            skCircle(sketch, "E79.10", {"center": v(-60, -67.5) * mm, "radius": 4 * mm});
            skCircle(sketch, "E79.11", {"center": v(60, -67.5) * mm, "radius": 4 * mm});
            skLineSegment(sketch, "E79.12", {"start": v(-60, 40.3) * mm, "end": v(-60, -40.3) * mm});
            skArc(sketch, "E79.13", {"start": v(-56.15, 48.18) * mm, "mid": v(-58.99, 44.68) * mm, "end": v(-60, 40.3) * mm});
            skArc(sketch, "E79.14", {"start": v(56.15, 48.18) * mm, "mid": v(0, 67.5) * mm, "end": v(-56.15, 48.18) * mm});
            skArc(sketch, "E79.15", {"start": v(60, 40.3) * mm, "mid": v(58.99, 44.68) * mm, "end": v(56.15, 48.18) * mm});
            skLineSegment(sketch, "E79.16", {"start": v(60, 40.3) * mm, "end": v(60, -40.3) * mm});
            skArc(sketch, "E79.17", {"start": v(56.15, -48.18) * mm, "mid": v(58.99, -44.68) * mm, "end": v(60, -40.3) * mm});
            skArc(sketch, "E79.18", {"start": v(-56.15, -48.18) * mm, "mid": v(0, -67.5) * mm, "end": v(56.15, -48.18) * mm});
            skArc(sketch, "E79.19", {"start": v(-60, -40.3) * mm, "mid": v(-58.99, -44.68) * mm, "end": v(-56.15, -48.18) * mm});
            skCircle(sketch, "E80", {"center": v(0, 120) * mm, "radius": 6 * mm});
            skLineSegment(sketch, "E81", {"start": v(-15, 120) * mm, "end": v(-15, 108) * mm});
            skLineSegment(sketch, "E82", {"start": v(-15, 108) * mm, "end": v(-33, 90) * mm});
            skArc(sketch, "E83", {"start": v(15, 120) * mm, "mid": v(0, 135) * mm, "end": v(-15, 120) * mm});
            skLineSegment(sketch, "E84", {"start": v(15, 120) * mm, "end": v(15, 108) * mm});
            skLineSegment(sketch, "E85", {"start": v(15, 108) * mm, "end": v(33, 90) * mm});
            skLineSegment(sketch, "E86", {"start": v(0, 23.75) * mm, "end": v(0, 90) * mm, "construction": true});
            skLineSegment(sketch, "E87", {"start": v(0, 120) * mm, "end": v(0, 90) * mm, "construction": true});
            skLineSegment(sketch, "E88", {"start": v(-80, 0) * mm, "end": v(80, 0) * mm, "construction": true});
            skCircle(sketch, "E89.MirrorC", {"center": v(0, -120) * mm, "radius": 6 * mm});
            skLineSegment(sketch, "E90.MirrorCS", {"start": v(-15, -108) * mm, "end": v(-33, -90) * mm});
            skLineSegment(sketch, "E91.MirrorCS", {"start": v(-15, -120) * mm, "end": v(-15, -108) * mm});
            skArc(sketch, "E92.MirrorCS", {"start": v(15, -120) * mm, "mid": v(0, -135) * mm, "end": v(-15, -120) * mm});
            skLineSegment(sketch, "E93.MirrorCS", {"start": v(15, -108) * mm, "end": v(33, -90) * mm});
            skLineSegment(sketch, "E94.MirrorCS", {"start": v(15, -120) * mm, "end": v(15, -108) * mm});
            skSolve(sketch);
        }
        {
            var Q0;
            Q0=makeQuery(id+"F16.imprint","IMPRINT",FACE,{"disambiguationData":[TD([[makeQuery(id+"F16.imprint","IMPRINT",EDGE,{"derivedFrom":sQuery(id+"F16.wireOp",EDGE,"E80")}),-1.0]])]});
            var Q1;
            {var subQ1=sQuery(id+"F16.wireOp",EDGE,"E79.1");Q1=makeQuery(id+"F16.imprint","IMPRINT",FACE,{"disambiguationData":[TD([[makeQuery(id+"F16.imprint","IMPRINT",EDGE,{"derivedFrom":subQ1}),1.0]])]});}
            var Q2;
            Q2=makeQuery(id+"F16.imprint","IMPRINT",FACE,{"disambiguationData":[TD([[makeQuery(id+"F16.imprint","IMPRINT",EDGE,{"derivedFrom":sQuery(id+"F16.wireOp",EDGE,"E89.MirrorC")}),1.0]])]});
            var Q3;
            Q3=makeQuery(id+"F2.opExtrude","CAP_FACE",FACE,{"disambiguationData":[OSD([sQuery(id+"F0.wireOp",EDGE,"E12"),sQuery(id+"F0.wireOp",EDGE,"E13"),sQuery(id+"F0.wireOp",EDGE,"E14"),sQuery(id+"F0.wireOp",EDGE,"E15"),sQuery(id+"F0.wireOp",EDGE,"E17.filletArc"),sQuery(id+"F0.wireOp",EDGE,"E18.filletArc"),sQuery(id+"F0.wireOp",EDGE,"E19.filletArc"),sQuery(id+"F0.wireOp",EDGE,"E20.filletArc"),sQuery(id+"F0.wireOp",EDGE,"E25.0"),sQuery(id+"F0.wireOp",EDGE,"E25.1"),sQuery(id+"F0.wireOp",EDGE,"E25.2"),sQuery(id+"F0.wireOp",EDGE,"E25.3"),sQuery(id+"F0.wireOp",EDGE,"E25.4"),sQuery(id+"F0.wireOp",EDGE,"E25.5"),sQuery(id+"F0.wireOp",EDGE,"E25.6"),sQuery(id+"F0.wireOp",EDGE,"E25.7")])],"isStart":false});
            extrude(context, id + "F17", {"entities" : qUnion([Q0, Q1, Q2]), "endBound" : BoundingType.UP_TO_SURFACE, "depth" : 25 * mm, "endBoundEntityFace" : qUnion([Q3]), "offsetDistance" : 25 * mm});
        }
    });
